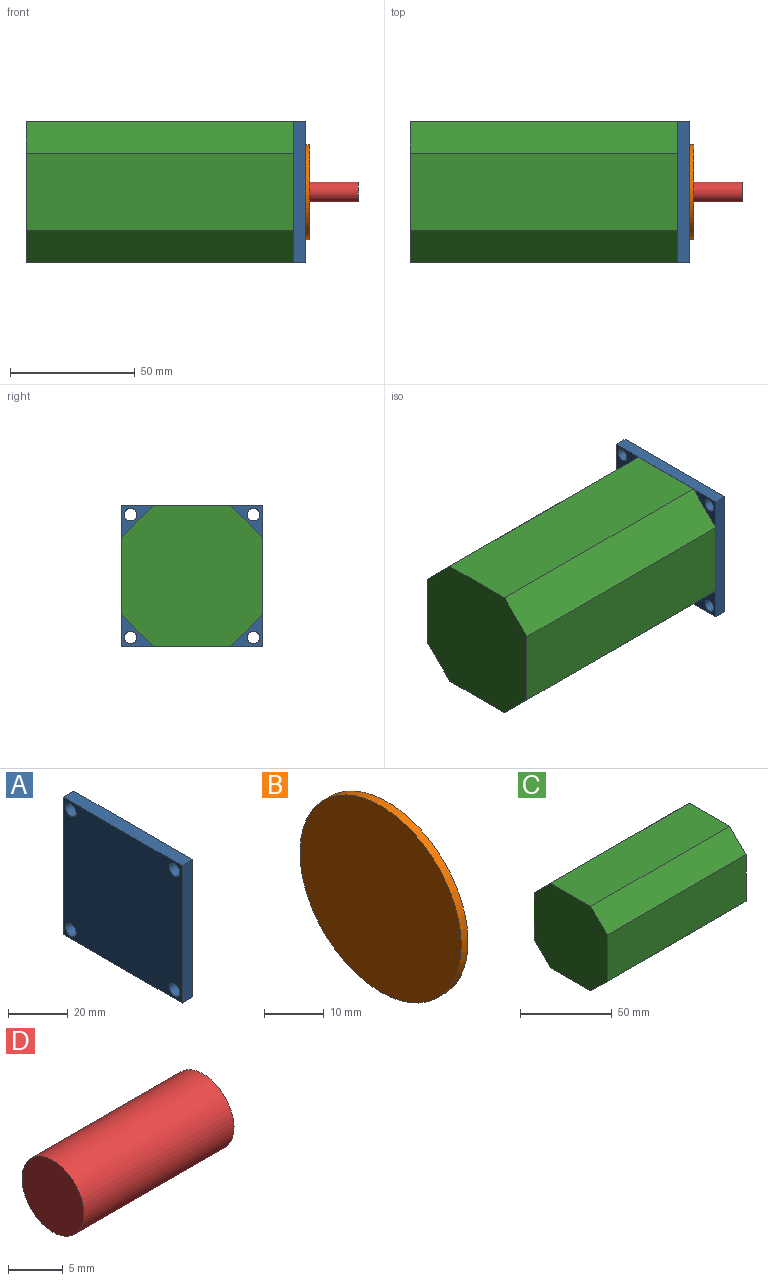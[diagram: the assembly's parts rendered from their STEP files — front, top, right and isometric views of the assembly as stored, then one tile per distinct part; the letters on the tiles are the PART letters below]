
ASSEMBLY  parts=4 mates=3
PART A: 10 faces, bbox 5x56.4x56.4 mm
  f0: plane 56.4x5mm, normal (0,0,1), area 282mm2, adj f1,f7,f8,f9
  f1: plane 56.4x5mm, normal (0,-1,0), area 282mm2, adj f0,f2,f8,f9
  f2: plane 56.4x5mm, normal (0,0,-1), area 282mm2, adj f1,f7,f8,f9
  f3: cylinder r=2.5mm len=5mm, axis (-1,0,0), area 78.5mm2, adj f8,f9
  f4: cylinder r=2.5mm len=5mm, axis (-1,0,0), area 78.5mm2, adj f8,f9
  f5: cylinder r=2.5mm len=5mm, axis (-1,0,0), area 78.5mm2, adj f8,f9
  f6: cylinder r=2.5mm len=5mm, axis (-1,0,0), area 78.5mm2, adj f8,f9
  f7: plane 56.4x5mm, normal (0,1,0), area 282mm2, adj f0,f2,f8,f9
  f8: plane 56.4x56.4mm, normal (1,0,0), area 3102.4mm2, adj f0,f1,f2,f3,f4,f5,f6,f7
  f9: plane 56.4x56.4mm, normal (-1,0,0), area 3102.4mm2, adj f0,f1,f2,f3,f4,f5,f6,f7
PART B: 3 faces, bbox 1.6x38.1x38.1 mm
  f0: cylinder r=19.05mm len=38.1mm, axis (-1,0,0), area 191.5mm2, adj f1,f2
  f1: plane 38.1x38.1mm, normal (1,0,0), area 1140.1mm2, adj f0
  f2: plane 38.1x38.1mm, normal (-1,0,0), area 1140.1mm2, adj f0
PART C: 10 faces, bbox 107x56.4x56.4 mm
  f0: plane 107x12.7mm, normal (0,0.71,0.71), area 1921.8mm2, adj f1,f7,f8,f9
  f1: plane 107x31mm, normal (0,0,1), area 3317mm2, adj f0,f2,f8,f9
  f2: plane 107x12.7mm, normal (0,-0.71,0.71), area 1921.8mm2, adj f1,f3,f8,f9
  f3: plane 107x31mm, normal (0,-1,0), area 3317mm2, adj f2,f4,f8,f9
  f4: plane 107x12.7mm, normal (0,-0.71,-0.71), area 1921.8mm2, adj f3,f5,f8,f9
  f5: plane 107x31mm, normal (0,0,-1), area 3317mm2, adj f4,f6,f8,f9
  f6: plane 107x12.7mm, normal (0,0.71,-0.71), area 1921.8mm2, adj f5,f7,f8,f9
  f7: plane 107x31mm, normal (0,1,0), area 3317mm2, adj f0,f6,f8,f9
  f8: plane 56.4x56.4mm, normal (1,0,0), area 2858.4mm2, adj f0,f1,f2,f3,f4,f5,f6,f7
  f9: plane 56.4x56.4mm, normal (-1,0,0), area 2858.4mm2, adj f0,f1,f2,f3,f4,f5,f6,f7
PART D: 3 faces, bbox 19.4x8x8 mm
  f0: cylinder r=4mm len=19.4mm, axis (-1,0,0), area 487.6mm2, adj f1,f2
  f1: plane 8x8mm, normal (1,0,0), area 50.3mm2, adj f0
  f2: plane 8x8mm, normal (-1,0,0), area 50.3mm2, adj f0
PLACE A t=(-73.65,-77.26,-35.75)mm
PLACE B t=(-68.65,-69.16,-25.46)mm
PLACE C t=(-180.65,-77.2,-35.75)mm
PLACE D t=(-67.05,-69.16,-25.46)mm
MATE fastened A.f8 <-> B.f0  axis (1,0,0) through (-68.65,-69.16,-25.46)mm
MATE fastened C.f8 <-> A.f9  axis (1,0,0) through (-73.65,-69.16,-25.46)mm
MATE fastened B.f0 <-> D.f0  axis (1,0,0) through (-67.05,-69.16,-25.46)mm
